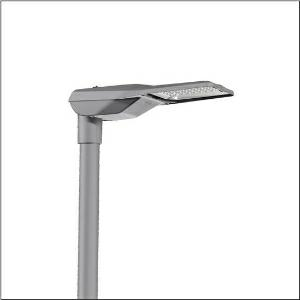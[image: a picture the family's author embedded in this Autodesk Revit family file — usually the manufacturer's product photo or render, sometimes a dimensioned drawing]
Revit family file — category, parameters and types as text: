
# Revit family: streetlight_sl_21_iq_mini___p0_5a_5xe2v31v08hb_1ab8
name_source: partatom
category: Lighting Fixtures
units: mm (PartAtom-declared; Revit-internal decimal feet)

## family parameters
Cut with Voids When Loaded = No
Host = Face
Light Source = No
Part Type = Normal
Room Calculation Point = No
Round Connector Dimension = Use Diameter
Shared = No

## types (1)
- --- (1 x LED, 9580 lm, 71 W, 3000K)
    Apparent Load = 71 VA
    CIE Flux Codes = 37 73 96 100 100
    Color Rendering = 70
    Color Temperature = 3000K
    Default Elevation = 1800 mm
    Description = Streetlight SL 21 iQ mini, mast luminaire, primary light control with lens, of PMMA, primary optical cover: cover, of toughened safety glass, transparent, light distribution: P0.5a, light emission: direct distribution, primary light characteristic: asymmetric, installation type: post-top, side-entry, LED, High Power LED, rated luminous flux: 9.580lm, luminous efficacy: 135lm/W, light colour: 730, colour temperature: 3000K, control gear: iQ-Street Remote, D4i with power reduction, control: pre-setting: logarithmic dimming characteristic, Street-Remote, Auto-Match, Temp-Guard, Lumen-Switch, Night-Set, Smart-Wire, Light-Fading, Desk-Remote (wireless, voltage-free reading and setting of iQ features in the workshop via application-optimized NFC function/RFID function), optimised constant luminous flux control (CLO 2.0), mains connection: 220..240V, AC, 50/60Hz, start of lifetime: 71W, end of service life: 75W, reduction: 30W, luminaire housing, of diecast aluminium, powder-coated, Siteco® metallic grey (DB 702S), corrosivity category C5 mid according to DIN EN ISO 12944, please order mast flange separately, inclination adjustable: 0°, 5°, 10°, 15°, sealing non-destructively replaceable, multi-level sealing system, length: 628mm, width: 235mm, height: 110mm, mast flange for spigot size: 42mm (side-entry): 5XC10008XM4, 60/48mm (side-entry/post-top): 5XC10108XM2, 76/60mm (side-entry/post-top): 5XC10108XM1, mounting height: 4..8m, Smart Interface above, protection rating (complete): IP66, insulation class (complete): insulation class II (safety insulation), certification: CE, ENEC, ENEC+, VDE, impact resistance: IK09, permissible operating ambient temperature for outdoor applications: -40..+50°C, standard-compliant lighting for roads and squares, packaging unit: 1 piece

Light Distribution: P0.5a
    Height = 110 mm
    Lamp = 1 x LED
    Lamp Light Flux = 9580 lm
    Lamp Power = 71 W
    Lamp count = 1
    Length = 625 mm
    Luminous efficacy = 135 lm/W
    Manufacturer = Siteco
    ModVariant = No
    Model = 5XE2V31V08HB
    Number of Poles = 1
    OnlyDefault = Yes
    Power Factor = 1
    Product Name = Streetlight SL 21 iQ mini | P0.5a
    Product group = mast luminaire | pylon top
    ProductGroupID = 6100
    Protection Class = Protection class II
    Protection Degree = IP 66
    RLX_Detail_Level = 1
    RLX_Emergency_Light_Flux = 0 lm
    RLX_Emergency_Type = 0
    RLX_Emergency_Type_DB = No
    RlxData = <blob elided: 91965 chars, md5=9e6ba4f1>
    Socket = socket
    Standby Power = 0 W
    System Light Flux = 9580 lm
    System Power = 71 W
    Type Comments = factory setting: luminous flux: 100 % | dim-lin: 254 | 716 mA
    Type Image = l_1003515.jpg
    URL = http://relux.com
    VarID = @adj_067564
    Voltage = 0 V
    Weight = 0.00 kg
    Width = 234 mm

## geometry (parser evidence)
native form markers: Blend x4, Sweep x10
no freeform markers — native parametric forms only
